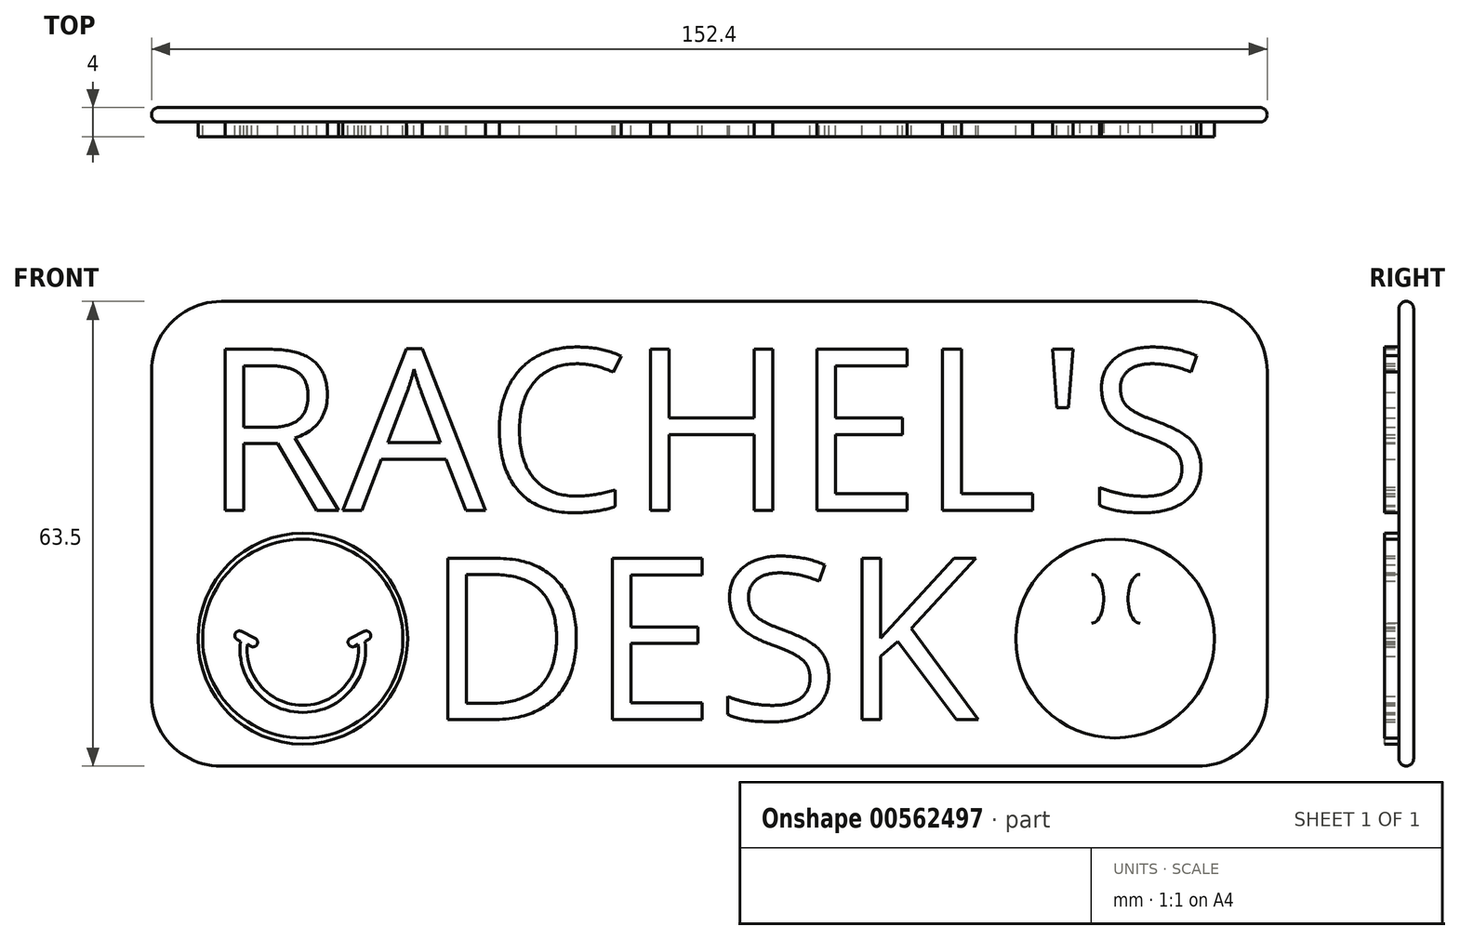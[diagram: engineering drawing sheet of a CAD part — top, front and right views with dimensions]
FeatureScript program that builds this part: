
annotation { "Feature Type Name" : "Feature", "Feature Type Description" : "" }
export const myFeature = defineFeature(function(context is Context, id is Id, definition is map)
    precondition{}
    {
        {
            var Q0;
            Q0=qCreatedBy(makeId("Front.planeOp"),FACE);
            var sketch = newSketch(context, id + "F0", { "sketchPlane" : qUnion([Q0])});
            skLineSegment(sketch, "E0.bottom", {"start": v(-76.2, 31.75) * mm, "end": v(76.2, 31.75) * mm});
            skLineSegment(sketch, "E0.top", {"start": v(-76.2, -31.75) * mm, "end": v(76.2, -31.75) * mm});
            skLineSegment(sketch, "E0.left", {"start": v(-76.2, 31.75) * mm, "end": v(-76.2, -31.75) * mm});
            skLineSegment(sketch, "E0.right", {"start": v(76.2, 31.75) * mm, "end": v(76.2, -31.75) * mm});
            skSolve(sketch);
        }
        {
            var Q0;
            Q0=qSketchRegion(id+"F0",true);
            extrude(context, id + "F1", {"entities" : qUnion([Q0]), "depth" : 2 * mm, "offsetDistance" : 25.4 * mm});
        }
        {
            var Q0;
            Q0=makeQuery(id+"F1.opExtrude","CAP_FACE",FACE,{"disambiguationData":[OSD([sQuery(id+"F0.wireOp",EDGE,"E0.bottom"),sQuery(id+"F0.wireOp",EDGE,"E0.top"),sQuery(id+"F0.wireOp",EDGE,"E0.left"),sQuery(id+"F0.wireOp",EDGE,"E0.right")])],"isStart":false});
            var sketch = newSketch(context, id + "F2", { "sketchPlane" : qUnion([Q0])});
            skText(sketch, "E1", { "text": "RACHEL\'S", "fontName": "OpenSans-Regular.ttf"});
            skText(sketch, "E2", { "text": "DESK", "fontName": "OpenSans-Regular.ttf"});
            const initialGuessF2  = {"E1": [-0.06917, 0.00317, 1, 0, 0.02222], "E2": [-0.03878, -0.0254, 1, 0, 0.02222]};
            skSetInitialGuess(sketch, initialGuessF2);
            skSolve(sketch);
        }
        {
            var Q0;
            Q0=qSketchRegion(id+"F2",true);
            extrude(context, id + "F3", {"entities" : qUnion([Q0]), "operationType" : NewBodyOperationType.ADD, "depth" : 2 * mm, "offsetDistance" : 25.4 * mm});
        }
        {
            var Q0;
            {var subQ0=sQuery(id+"F0.wireOp",EDGE,"E0.top");var subQ1=sQuery(id+"F0.wireOp",EDGE,"E0.right");var subQ2=sQuery(id+"F0.wireOp",EDGE,"E0.bottom");var subQ3=sQuery(id+"F0.wireOp",EDGE,"E0.left");Q0=makeQuery(id+"F3.boolean.opBoolean","SPLIT",FACE,{"disambiguationData":[TD([makeQuery(id+"F1.opExtrude","SWEPT_FACE",FACE,{"disambiguationData":[OSD([subQ2])]})])],"derivedFrom":makeQuery(id+"F1.opExtrude","CAP_FACE",FACE,{"disambiguationData":[OSD([subQ2,subQ0,subQ3,subQ1])],"isStart":false})});}
            var sketch = newSketch(context, id + "F4", { "sketchPlane" : qUnion([Q0])});
            skCircle(sketch, "E3", {"center": v(-55.42, -14.33) * mm, "radius": 14.43 * mm});
            skPoint(sketch, "E3.first.point", {"position": v(-65.71, -4.21) * mm});
            skPoint(sketch, "E3.second.point", {"position": v(-44.72, -4.65) * mm});
            skPoint(sketch, "E3.third.point", {"position": v(-46.22, -25.45) * mm});
            skCircle(sketch, "E4", {"center": v(-55.42, -14.33) * mm, "radius": 13.57 * mm});
            skArc(sketch, "E5", {"start": v(-63.1, -15.1) * mm, "mid": v(-55.53, -23.45) * mm, "end": v(-47.96, -15.1) * mm});
            skArc(sketch, "E6", {"start": v(-64.04, -14.71) * mm, "mid": v(-55.53, -24.42) * mm, "end": v(-47.02, -14.71) * mm});
            skPoint(sketch, "E7.first.point", {"position": v(-64.3, -13.39) * mm});
            skPoint(sketch, "E7.second.point", {"position": v(-64.78, -13.7) * mm});
            skPoint(sketch, "E7.third.point", {"position": v(-64.81, -14.11) * mm});
            skLineSegment(sketch, "E8", {"start": v(-64.04, -14.71) * mm, "end": v(-64.49, -14.47) * mm});
            skArc(sketch, "E9", {"start": v(-63.9, -13.34) * mm, "mid": v(-64.75, -13.62) * mm, "end": v(-64.49, -14.47) * mm});
            skLineSegment(sketch, "E10", {"start": v(-63.9, -13.34) * mm, "end": v(-62.06, -14.25) * mm});
            skArc(sketch, "E11", {"start": v(-62.54, -15.42) * mm, "mid": v(-61.75, -15.06) * mm, "end": v(-62.06, -14.25) * mm});
            skLineSegment(sketch, "E12", {"start": v(-63.1, -15.1) * mm, "end": v(-62.54, -15.42) * mm});
            skLineSegment(sketch, "E13", {"start": v(-55.53, -15.84) * mm, "end": v(-55.53, -20.86) * mm, "construction": true});
            skLineSegment(sketch, "E14.MirrorCS", {"start": v(-47.02, -14.71) * mm, "end": v(-46.57, -14.47) * mm});
            skArc(sketch, "E15.MirrorCS", {"start": v(-47.15, -13.34) * mm, "mid": v(-46.3, -13.62) * mm, "end": v(-46.57, -14.47) * mm});
            skLineSegment(sketch, "E16.MirrorCS", {"start": v(-47.96, -15.1) * mm, "end": v(-48.51, -15.42) * mm});
            skLineSegment(sketch, "E17.MirrorCS", {"start": v(-47.15, -13.34) * mm, "end": v(-49, -14.25) * mm});
            skArc(sketch, "E18.MirrorCS", {"start": v(-48.51, -15.42) * mm, "mid": v(-49.3, -15.06) * mm, "end": v(-49, -14.25) * mm});
            skEllipse(sketch, "E19", {"center": v(-58.8, -8.89) * mm, "majorRadius": 3.34 * mm, "minorRadius": 1.61 * mm, "majorAxis": v(0, 1)});
            skEllipse(sketch, "E20", {"center": v(-52.19, -8.89) * mm, "majorRadius": 3.34 * mm, "minorRadius": 1.61 * mm, "majorAxis": v(0, 1)});
            skPoint(sketch, "E21.MirrorP", {"position": v(-46.75, -13.39) * mm});
            skArc(sketch, "E22.MirrorCS", {"start": v(-47.96, -15.1) * mm, "mid": v(-55.53, -23.45) * mm, "end": v(-63.1, -15.1) * mm});
            skEllipse(sketch, "E23.MirrorC", {"center": v(-52.26, -8.89) * mm, "majorRadius": 3.34 * mm, "minorRadius": 1.61 * mm, "majorAxis": v(0, 1)});
            skPoint(sketch, "E24.MirrorP", {"position": v(-66.33, -4.65) * mm});
            skArc(sketch, "E25.MirrorCS", {"start": v(-47.02, -14.71) * mm, "mid": v(-55.53, -24.42) * mm, "end": v(-64.04, -14.71) * mm});
            skCircle(sketch, "E26.MirrorC", {"center": v(-55.63, -14.33) * mm, "radius": 13.57 * mm});
            skCircle(sketch, "E27.MirrorC", {"center": v(-55.63, -14.33) * mm, "radius": 14.43 * mm});
            skPoint(sketch, "E28.MirrorP", {"position": v(-46.28, -13.7) * mm});
            skPoint(sketch, "E29.MirrorP", {"position": v(-46.24, -14.11) * mm});
            skEllipse(sketch, "E30.MirrorC", {"center": v(-58.87, -8.89) * mm, "majorRadius": 3.34 * mm, "minorRadius": 1.61 * mm, "majorAxis": v(0, 1)});
            skPoint(sketch, "E31.MirrorP", {"position": v(-64.83, -25.45) * mm});
            skPoint(sketch, "E32.MirrorP", {"position": v(-45.34, -4.21) * mm});
            skEllipse(sketch, "E33.MirrorC", {"center": v(-58.8, -8.89) * mm, "majorRadius": 3.34 * mm, "minorRadius": 1.61 * mm, "majorAxis": v(0, 1)});
            skEllipse(sketch, "E34.MirrorC", {"center": v(-52.26, -8.89) * mm, "majorRadius": 3.34 * mm, "minorRadius": 1.61 * mm, "majorAxis": v(0, 1)});
            skEllipse(sketch, "E35.MirrorC", {"center": v(-58.87, -8.89) * mm, "majorRadius": 3.34 * mm, "minorRadius": 1.61 * mm, "majorAxis": v(0, 1)});
            skEllipse(sketch, "E36.MirrorC", {"center": v(-52.19, -8.89) * mm, "majorRadius": 3.34 * mm, "minorRadius": 1.61 * mm, "majorAxis": v(0, 1)});
            skEllipse(sketch, "E37.MirrorC", {"center": v(58.8, -8.89) * mm, "majorRadius": 3.34 * mm, "minorRadius": 1.61 * mm, "majorAxis": v(0, 1)});
            skEllipse(sketch, "E38.MirrorC", {"center": v(58.87, -8.89) * mm, "majorRadius": 3.34 * mm, "minorRadius": 1.61 * mm, "majorAxis": v(0, 1)});
            skEllipse(sketch, "E39.MirrorC", {"center": v(52.26, -8.89) * mm, "majorRadius": 3.34 * mm, "minorRadius": 1.61 * mm, "majorAxis": v(0, 1)});
            skEllipse(sketch, "E40.MirrorC", {"center": v(52.19, -8.89) * mm, "majorRadius": 3.34 * mm, "minorRadius": 1.61 * mm, "majorAxis": v(0, 1)});
            skEllipse(sketch, "E41.MirrorC", {"center": v(58.87, -8.89) * mm, "majorRadius": 3.34 * mm, "minorRadius": 1.61 * mm, "majorAxis": v(0, 1)});
            skEllipse(sketch, "E42.MirrorC", {"center": v(52.19, -8.89) * mm, "majorRadius": 3.34 * mm, "minorRadius": 1.61 * mm, "majorAxis": v(0, 1)});
            skEllipse(sketch, "E43.MirrorC", {"center": v(58.8, -8.89) * mm, "majorRadius": 3.34 * mm, "minorRadius": 1.61 * mm, "majorAxis": v(0, 1)});
            skEllipse(sketch, "E44.MirrorC", {"center": v(52.26, -8.89) * mm, "majorRadius": 3.34 * mm, "minorRadius": 1.61 * mm, "majorAxis": v(0, 1)});
            skLineSegment(sketch, "E45.MirrorCS", {"start": v(47.02, -14.71) * mm, "end": v(46.57, -14.47) * mm});
            skLineSegment(sketch, "E46.MirrorCS", {"start": v(47.96, -15.1) * mm, "end": v(48.51, -15.42) * mm});
            skLineSegment(sketch, "E47.MirrorCS", {"start": v(64.04, -14.71) * mm, "end": v(64.49, -14.47) * mm});
            skLineSegment(sketch, "E48.MirrorCS", {"start": v(63.1, -15.1) * mm, "end": v(62.54, -15.42) * mm});
            skArc(sketch, "E49.MirrorCS", {"start": v(47.15, -13.34) * mm, "mid": v(46.3, -13.62) * mm, "end": v(46.57, -14.47) * mm});
            skArc(sketch, "E50.MirrorCS", {"start": v(63.9, -13.34) * mm, "mid": v(64.75, -13.62) * mm, "end": v(64.49, -14.47) * mm});
            skLineSegment(sketch, "E51.MirrorCS", {"start": v(63.9, -13.34) * mm, "end": v(62.06, -14.25) * mm});
            skArc(sketch, "E52.MirrorCS", {"start": v(48.51, -15.42) * mm, "mid": v(49.3, -15.06) * mm, "end": v(49, -14.25) * mm});
            skArc(sketch, "E53.MirrorCS", {"start": v(62.54, -15.42) * mm, "mid": v(61.75, -15.06) * mm, "end": v(62.06, -14.25) * mm});
            skLineSegment(sketch, "E54.MirrorCS", {"start": v(47.15, -13.34) * mm, "end": v(49, -14.25) * mm});
            skArc(sketch, "E55.MirrorCS", {"start": v(63.1, -15.1) * mm, "mid": v(55.53, -23.45) * mm, "end": v(47.96, -15.1) * mm});
            skPoint(sketch, "E56.MirrorP", {"position": v(46.28, -13.7) * mm});
            skPoint(sketch, "E57.MirrorP", {"position": v(46.24, -14.11) * mm});
            skPoint(sketch, "E58.MirrorP", {"position": v(64.3, -13.39) * mm});
            skArc(sketch, "E59.MirrorCS", {"start": v(47.02, -14.71) * mm, "mid": v(55.53, -24.42) * mm, "end": v(64.04, -14.71) * mm});
            skPoint(sketch, "E60.MirrorP", {"position": v(64.81, -14.11) * mm});
            skPoint(sketch, "E61.MirrorP", {"position": v(64.78, -13.7) * mm});
            skPoint(sketch, "E62.MirrorP", {"position": v(46.75, -13.39) * mm});
            skArc(sketch, "E63.MirrorCS", {"start": v(47.96, -15.1) * mm, "mid": v(55.53, -23.45) * mm, "end": v(63.1, -15.1) * mm});
            skArc(sketch, "E64.MirrorCS", {"start": v(64.04, -14.71) * mm, "mid": v(55.53, -24.42) * mm, "end": v(47.02, -14.71) * mm});
            skLineSegment(sketch, "E65.MirrorCS", {"start": v(55.53, -15.84) * mm, "end": v(55.53, -20.86) * mm, "construction": true});
            skCircle(sketch, "E66.MirrorC", {"center": v(55.42, -14.33) * mm, "radius": 13.57 * mm});
            skCircle(sketch, "E67.MirrorC", {"center": v(55.42, -14.33) * mm, "radius": 14.43 * mm});
            skSolve(sketch);
        }
        {
            var Q0;
            Q0=makeQuery(id+"F4.imprint","IMPRINT",FACE,{"disambiguationData":[TD([[makeQuery(id+"F4.imprint","IMPRINT",EDGE,{"derivedFrom":sQuery(id+"F4.wireOp",EDGE,"E66.MirrorC")}),1.0]])]});
            var Q1;
            {var subQ0=sQuery(id+"F4.wireOp",EDGE,"E43.MirrorC");var subQ1=sQuery(id+"F4.wireOp",EDGE,"E41.MirrorC");var subQ2=makeQuery(id+"F4.imprint","INTERSECT",VERTEX,{"disambiguationData":[OD(0.0)],"derivedFrom":[subQ1,subQ0]});Q1=makeQuery(id+"F4.imprint","IMPRINT",FACE,{"disambiguationData":[TD([[makeQuery(id+"F4.imprint","IMPRINT",EDGE,{"disambiguationData":[TD([[subQ2,1.0]])],"derivedFrom":subQ1}),1.0]])]});}
            var Q2;
            {var subQ0=sQuery(id+"F4.wireOp",EDGE,"E44.MirrorC");var subQ1=sQuery(id+"F4.wireOp",EDGE,"E42.MirrorC");var subQ2=makeQuery(id+"F4.imprint","INTERSECT",VERTEX,{"disambiguationData":[OD(0.0)],"derivedFrom":[subQ1,subQ0]});Q2=makeQuery(id+"F4.imprint","IMPRINT",FACE,{"disambiguationData":[TD([[makeQuery(id+"F4.imprint","IMPRINT",EDGE,{"disambiguationData":[TD([[subQ2,-1.0]])],"derivedFrom":subQ1}),1.0]])]});}
            var Q3;
            Q3=makeQuery(id+"F4.imprint","IMPRINT",FACE,{"disambiguationData":[TD([[makeQuery(id+"F4.imprint","IMPRINT",EDGE,{"derivedFrom":sQuery(id+"F4.wireOp",EDGE,"E47.MirrorCS")}),1.0]])]});
            var Q4;
            {var subQ0=sQuery(id+"F4.wireOp",EDGE,"E27.MirrorC");var subQ1=sQuery(id+"F4.wireOp",EDGE,"E3");var subQ2=makeQuery(id+"F4.imprint","INTERSECT",VERTEX,{"disambiguationData":[OD(0.0)],"derivedFrom":[subQ1,subQ0]});Q4=makeQuery(id+"F4.imprint","IMPRINT",FACE,{"disambiguationData":[TD([[makeQuery(id+"F4.imprint","IMPRINT",EDGE,{"disambiguationData":[TD([[subQ2,1.0]])],"derivedFrom":subQ1}),1.0]])]});}
            var Q5;
            {var subQ0=sQuery(id+"F4.wireOp",EDGE,"E36.MirrorC");var subQ1=sQuery(id+"F4.wireOp",EDGE,"E34.MirrorC");var subQ2=makeQuery(id+"F4.imprint","INTERSECT",VERTEX,{"disambiguationData":[OD(0.0)],"derivedFrom":[subQ1,subQ0]});Q5=makeQuery(id+"F4.imprint","IMPRINT",FACE,{"disambiguationData":[TD([[makeQuery(id+"F4.imprint","IMPRINT",EDGE,{"disambiguationData":[TD([[subQ2,-1.0]])],"derivedFrom":subQ1}),1.0]])]});}
            var Q6;
            {var subQ0=sQuery(id+"F4.wireOp",EDGE,"E35.MirrorC");var subQ1=sQuery(id+"F4.wireOp",EDGE,"E33.MirrorC");var subQ2=makeQuery(id+"F4.imprint","INTERSECT",VERTEX,{"disambiguationData":[OD(0.0)],"derivedFrom":[subQ1,subQ0]});Q6=makeQuery(id+"F4.imprint","IMPRINT",FACE,{"disambiguationData":[TD([[makeQuery(id+"F4.imprint","IMPRINT",EDGE,{"disambiguationData":[TD([[subQ2,1.0]])],"derivedFrom":subQ1}),1.0]])]});}
            var Q7;
            Q7=makeQuery(id+"F4.imprint","IMPRINT",FACE,{"disambiguationData":[TD([[makeQuery(id+"F4.imprint","IMPRINT",EDGE,{"derivedFrom":sQuery(id+"F4.wireOp",EDGE,"E14.MirrorCS")}),1.0]])]});
            extrude(context, id + "F5", {"entities" : qUnion([Q0, Q1, Q2, Q3, Q4, Q5, Q6, Q7]), "operationType" : NewBodyOperationType.ADD, "depth" : 2 * mm, "offsetDistance" : 25.4 * mm});
        }
        {
            var Q0;
            Q0=makeQuery(id+"F1.opExtrude","SWEPT_EDGE",EDGE,{"disambiguationData":[OSD([sQuery(id+"F0.wireOp",EDGE,"E0.bottom"),sQuery(id+"F0.wireOp",EDGE,"E0.right")])]});
            var Q1;
            Q1=makeQuery(id+"F1.opExtrude","SWEPT_EDGE",EDGE,{"disambiguationData":[OSD([sQuery(id+"F0.wireOp",EDGE,"E0.top"),sQuery(id+"F0.wireOp",EDGE,"E0.right")])]});
            var Q2;
            Q2=makeQuery(id+"F1.opExtrude","SWEPT_EDGE",EDGE,{"disambiguationData":[OSD([sQuery(id+"F0.wireOp",EDGE,"E0.bottom"),sQuery(id+"F0.wireOp",EDGE,"E0.left")])]});
            var Q3;
            Q3=makeQuery(id+"F1.opExtrude","SWEPT_EDGE",EDGE,{"disambiguationData":[OSD([sQuery(id+"F0.wireOp",EDGE,"E0.top"),sQuery(id+"F0.wireOp",EDGE,"E0.left")])]});
            fillet(context, id + "F6", {"entities" : qUnion([Q0, Q1, Q2, Q3]), "radius" : 9.52 * mm, "tangentPropagation" : true, "allowEdgeOverflow" : false});
        }
        {
            var Q0;
            Q0=makeQuery(id+"F1.opExtrude","CAP_EDGE",EDGE,{"disambiguationData":[OSD([sQuery(id+"F0.wireOp",EDGE,"E0.top")])],"isStart":false});
            var Q1;
            Q1=makeQuery(id+"F1.opExtrude","CAP_EDGE",EDGE,{"disambiguationData":[OSD([sQuery(id+"F0.wireOp",EDGE,"E0.top")])],"isStart":true});
            var Q2;
            Q2=makeQuery(id+"F1.opExtrude","CAP_EDGE",EDGE,{"disambiguationData":[OSD([sQuery(id+"F0.wireOp",EDGE,"E0.left")])],"isStart":false});
            var Q3;
            Q3=makeQuery(id+"F1.opExtrude","CAP_EDGE",EDGE,{"disambiguationData":[OSD([sQuery(id+"F0.wireOp",EDGE,"E0.left")])],"isStart":true});
            var Q4;
            Q4=makeQuery(id+"F1.opExtrude","SWEPT_EDGE",EDGE,{"disambiguationData":[OSD([sQuery(id+"F0.wireOp",EDGE,"E0.top"),sQuery(id+"F0.wireOp",EDGE,"E0.left")])]});
            var Q5;
            Q5=makeQuery(id+"F1.opExtrude","SWEPT_EDGE",EDGE,{"disambiguationData":[OSD([sQuery(id+"F0.wireOp",EDGE,"E0.bottom"),sQuery(id+"F0.wireOp",EDGE,"E0.left")])]});
            var Q6;
            Q6=makeQuery(id+"F1.opExtrude","CAP_EDGE",EDGE,{"disambiguationData":[OSD([sQuery(id+"F0.wireOp",EDGE,"E0.bottom")])],"isStart":false});
            var Q7;
            Q7=makeQuery(id+"F1.opExtrude","CAP_EDGE",EDGE,{"disambiguationData":[OSD([sQuery(id+"F0.wireOp",EDGE,"E0.bottom")])],"isStart":true});
            var Q8;
            Q8=makeQuery(id+"F1.opExtrude","SWEPT_EDGE",EDGE,{"disambiguationData":[OSD([sQuery(id+"F0.wireOp",EDGE,"E0.bottom"),sQuery(id+"F0.wireOp",EDGE,"E0.right")])]});
            var Q9;
            Q9=makeQuery(id+"F1.opExtrude","CAP_EDGE",EDGE,{"disambiguationData":[OSD([sQuery(id+"F0.wireOp",EDGE,"E0.right")])],"isStart":true});
            var Q10;
            Q10=makeQuery(id+"F1.opExtrude","CAP_EDGE",EDGE,{"disambiguationData":[OSD([sQuery(id+"F0.wireOp",EDGE,"E0.right")])],"isStart":false});
            var Q11;
            Q11=makeQuery(id+"F1.opExtrude","SWEPT_EDGE",EDGE,{"disambiguationData":[OSD([sQuery(id+"F0.wireOp",EDGE,"E0.top"),sQuery(id+"F0.wireOp",EDGE,"E0.right")])]});
            fillet(context, id + "F7", {"entities" : qUnion([Q0, Q1, Q2, Q3, Q4, Q5, Q6, Q7, Q8, Q9, Q10, Q11]), "radius" : 1 * mm, "tangentPropagation" : true, "allowEdgeOverflow" : false});
        }
    });
